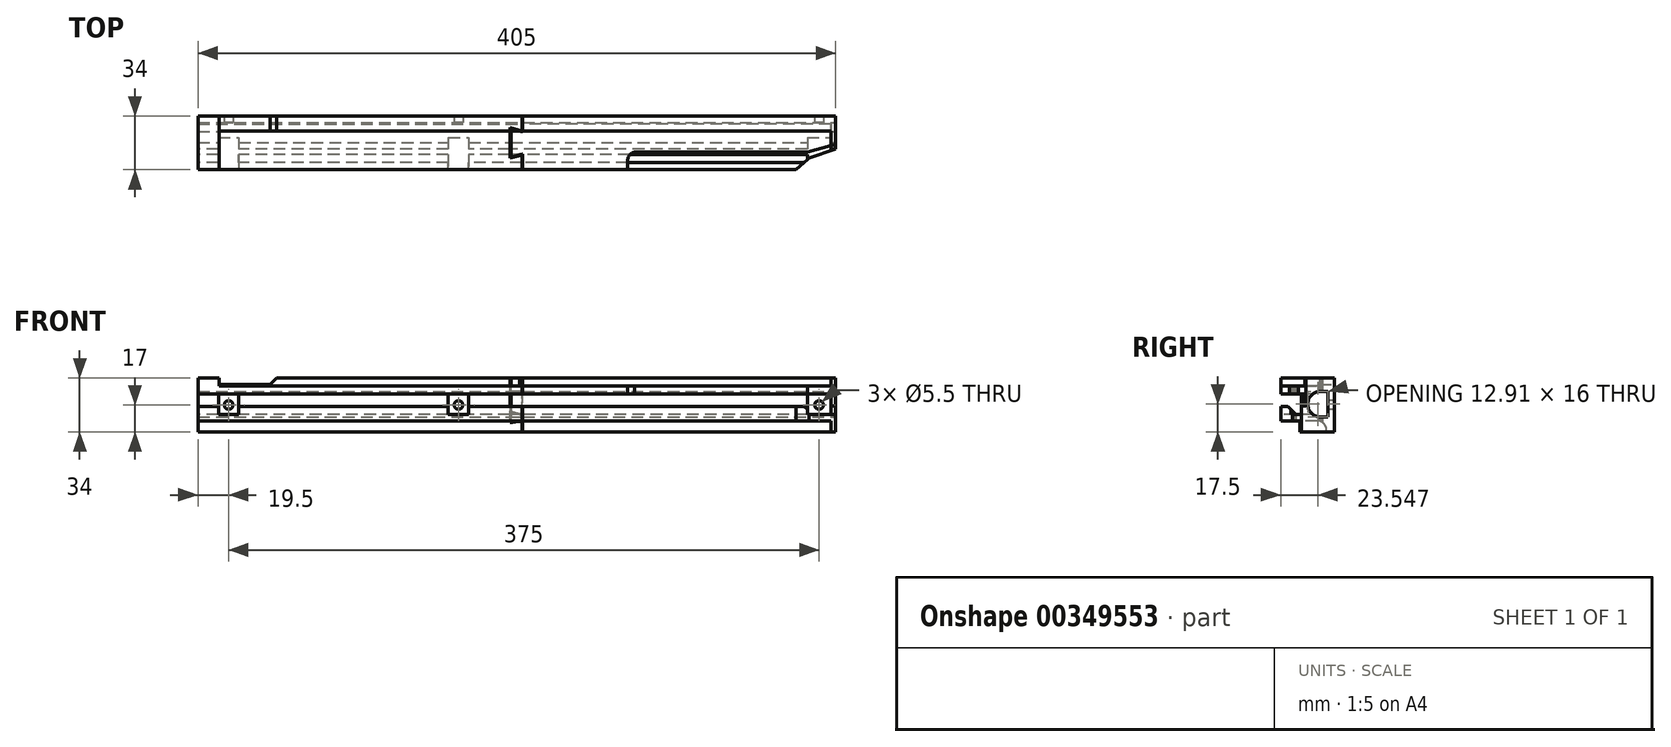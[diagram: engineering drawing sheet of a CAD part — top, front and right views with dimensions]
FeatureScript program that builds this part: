
annotation { "Feature Type Name" : "Feature", "Feature Type Description" : "" }
export const myFeature = defineFeature(function(context is Context, id is Id, definition is map)
    precondition{}
    {
        {
            var Q0;
            Q0=qCreatedBy(makeId("Front.planeOp"),FACE);
            var sketch = newSketch(context, id + "F0", { "sketchPlane" : qUnion([Q0])});
            skLineSegment(sketch, "E0.bottom", {"start": v(202.5, -17) * mm, "end": v(-202.5, -17) * mm});
            skLineSegment(sketch, "E0.top", {"start": v(202.5, 17) * mm, "end": v(-202.5, 17) * mm});
            skLineSegment(sketch, "E0.left", {"start": v(202.5, -17) * mm, "end": v(202.5, 17) * mm});
            skLineSegment(sketch, "E0.right", {"start": v(-202.5, -17) * mm, "end": v(-202.5, 17) * mm});
            skPoint(sketch, "E0.middle", {"position": v(0, 0) * mm});
            skSolve(sketch);
        }
        {
            var Q0;
            Q0 = qSketchRegion(id + "F0", true);
            extrude(context, id + "F1", {"entities" : qUnion([Q0]), "depth" : 34 * mm});
        }
        {
            var Q0;
            Q0=makeQuery(id+"F1.opExtrude","CAP_FACE",FACE,{"disambiguationData":[OSD([sQuery(id+"F0.wireOp",EDGE,"E0.bottom"),sQuery(id+"F0.wireOp",EDGE,"E0.top"),sQuery(id+"F0.wireOp",EDGE,"E0.left"),sQuery(id+"F0.wireOp",EDGE,"E0.right")])],"isStart":false});
            var sketch = newSketch(context, id + "F2", { "sketchPlane" : qUnion([Q0])});
            skLineSegment(sketch, "E1.bottom", {"start": v(-202.5, -17) * mm, "end": v(199.5, -17) * mm});
            skLineSegment(sketch, "E1.top", {"start": v(-202.5, -10) * mm, "end": v(199.5, -10) * mm});
            skLineSegment(sketch, "E1.left", {"start": v(-202.5, -17) * mm, "end": v(-202.5, -10) * mm});
            skLineSegment(sketch, "E2", {"start": v(199.5, -10) * mm, "end": v(199.5, -17) * mm});
            skSolve(sketch);
        }
        {
            var Q0;
            Q0 = qSketchRegion(id + "F2", true);
            extrude(context, id + "F3", {"entities" : qUnion([Q0]), "operationType" : NewBodyOperationType.REMOVE, "oppositeDirection" : true, "depth" : 29 * mm});
        }
        {
            var Q0;
            Q0=makeQuery(id+"F1.opExtrude","CAP_FACE",FACE,{"disambiguationData":[OSD([sQuery(id+"F0.wireOp",EDGE,"E0.bottom"),sQuery(id+"F0.wireOp",EDGE,"E0.top"),sQuery(id+"F0.wireOp",EDGE,"E0.left"),sQuery(id+"F0.wireOp",EDGE,"E0.right")])],"isStart":false});
            var sketch = newSketch(context, id + "F4", { "sketchPlane" : qUnion([Q0])});
            skLineSegment(sketch, "E3.bottom", {"start": v(-189, 17) * mm, "end": v(193, 17) * mm});
            skLineSegment(sketch, "E3.top", {"start": v(-189, 12) * mm, "end": v(193, 12) * mm});
            skLineSegment(sketch, "E3.left", {"start": v(-189, 17) * mm, "end": v(-189, 12) * mm});
            skLineSegment(sketch, "E3.right", {"start": v(193, 17) * mm, "end": v(193, 12) * mm});
            skSolve(sketch);
        }
        {
            var Q0;
            Q0 = qSketchRegion(id + "F4", true);
            extrude(context, id + "F5", {"entities" : qUnion([Q0]), "operationType" : NewBodyOperationType.REMOVE, "oppositeDirection" : true, "depth" : 24.5 * mm});
        }
        {
            var Q0;
            Q0=makeQuery(id+"F3.boolean.opBoolean","COPY",EDGE,{"derivedFrom":makeQuery(id+"F3.opExtrude","CAP_EDGE",EDGE,{"disambiguationData":[OSD([sQuery(id+"F2.wireOp",EDGE,"E1.top")])],"isStart":false})});
            fillet(context, id + "F6", {"entities" : qUnion([Q0]), "radius" : 6 * mm, "tangentPropagation" : true, "allowEdgeOverflow" : false});
        }
        {
            var Q0;
            Q0=makeQuery(id+"F1.opExtrude","SWEPT_FACE",FACE,{"disambiguationData":[OSD([sQuery(id+"F0.wireOp",EDGE,"E0.right")])]});
            var sketch = newSketch(context, id + "F7", { "sketchPlane" : qUnion([Q0])});
            skLineSegment(sketch, "E4", {"start": v(34, 7) * mm, "end": v(21, 7) * mm});
            skLineSegment(sketch, "E5", {"start": v(21, 7) * mm, "end": v(21, -6) * mm});
            skLineSegment(sketch, "E6", {"start": v(21, -6) * mm, "end": v(24.5, -6) * mm});
            skLineSegment(sketch, "E7", {"start": v(24.5, -6) * mm, "end": v(29.5, -1) * mm});
            skLineSegment(sketch, "E8", {"start": v(34, -1) * mm, "end": v(29.5, -1) * mm});
            skLineSegment(sketch, "E9", {"start": v(34, 7) * mm, "end": v(34, -1) * mm});
            skSolve(sketch);
        }
        {
            var Q0;
            Q0 = qSketchRegion(id + "F7", true);
            extrude(context, id + "F8", {"entities" : qUnion([Q0]), "operationType" : NewBodyOperationType.REMOVE, "endBound" : BoundingType.THROUGH_ALL, "oppositeDirection" : true, "depth" : 25 * mm});
        }
        {
            var Q0;
            Q0=makeQuery(id+"F1.opExtrude","CAP_FACE",FACE,{"disambiguationData":[OSD([sQuery(id+"F0.wireOp",EDGE,"E0.bottom"),sQuery(id+"F0.wireOp",EDGE,"E0.top"),sQuery(id+"F0.wireOp",EDGE,"E0.left"),sQuery(id+"F0.wireOp",EDGE,"E0.right")])],"isStart":true});
            var sketch = newSketch(context, id + "F9", { "sketchPlane" : qUnion([Q0])});
            skLineSegment(sketch, "E10.bottom", {"start": v(189, 17) * mm, "end": v(155.21, 17) * mm});
            skLineSegment(sketch, "E10.top", {"start": v(189, 13) * mm, "end": v(156.5, 13) * mm});
            skLineSegment(sketch, "E10.left", {"start": v(189, 17) * mm, "end": v(189, 13) * mm});
            skLineSegment(sketch, "E11", {"start": v(156.5, 13) * mm, "end": v(152.5, 17) * mm});
            skLineSegment(sketch, "E12", {"start": v(155.21, 17) * mm, "end": v(152.5, 17) * mm});
            skSolve(sketch);
        }
        {
            var Q0;
            Q0 = qSketchRegion(id + "F9", true);
            extrude(context, id + "F10", {"entities" : qUnion([Q0]), "operationType" : NewBodyOperationType.REMOVE, "endBound" : BoundingType.THROUGH_ALL, "oppositeDirection" : true, "depth" : 25 * mm});
        }
        {
            var Q0;
            {var subQ0=sQuery(id+"F0.wireOp",EDGE,"E0.left");var subQ1=sQuery(id+"F0.wireOp",EDGE,"E0.right");var subQ2=sQuery(id+"F0.wireOp",EDGE,"E0.bottom");Q0=makeQuery(id+"F8.boolean.opBoolean","SPLIT",FACE,{"disambiguationData":[TD([makeQuery(id+"F1.opExtrude","SWEPT_FACE",FACE,{"disambiguationData":[OSD([subQ2])]})])],"derivedFrom":makeQuery(id+"F1.opExtrude","CAP_FACE",FACE,{"disambiguationData":[OSD([subQ2,sQuery(id+"F0.wireOp",EDGE,"E0.top"),subQ0,subQ1])],"isStart":false})});}
            var sketch = newSketch(context, id + "F11", { "sketchPlane" : qUnion([Q0])});
            skLineSegment(sketch, "E13.bottom", {"start": v(-189.5, 7) * mm, "end": v(-176.5, 7) * mm});
            skLineSegment(sketch, "E13.top", {"start": v(-189.5, -6) * mm, "end": v(-176.5, -6) * mm});
            skLineSegment(sketch, "E13.left", {"start": v(-189.5, 7) * mm, "end": v(-189.5, -6) * mm});
            skLineSegment(sketch, "E13.right", {"start": v(-176.5, 7) * mm, "end": v(-176.5, -6) * mm});
            skSolve(sketch);
        }
        {
            var Q0;
            Q0 = qSketchRegion(id + "F11", true);
            extrude(context, id + "F12", {"entities" : qUnion([Q0]), "operationType" : NewBodyOperationType.REMOVE, "oppositeDirection" : true, "depth" : 30 * mm});
        }
        {
            var Q0;
            Q0=makeQuery(id+"F12.boolean.opBoolean","COPY",FACE,{"derivedFrom":makeQuery(id+"F12.opExtrude","CAP_FACE",FACE,{"disambiguationData":[OSD([sQuery(id+"F11.wireOp",EDGE,"E13.bottom"),sQuery(id+"F11.wireOp",EDGE,"E13.top"),sQuery(id+"F11.wireOp",EDGE,"E13.left"),sQuery(id+"F11.wireOp",EDGE,"E13.right")])],"isStart":false})});
            var sketch = newSketch(context, id + "F13", { "sketchPlane" : qUnion([Q0])});
            skLineSegment(sketch, "E14", {"start": v(-176.5, -6) * mm, "end": v(-176.5, 7) * mm, "construction": true});
            skLineSegment(sketch, "E15", {"start": v(-176.5, 0) * mm, "end": v(-185.96, 0) * mm, "construction": true});
            skPoint(sketch, "E16.trimOffspring.end.orphan", {"position": v(-189.5, -6) * mm});
            skPoint(sketch, "E17.orphan", {"position": v(-172.63, 0) * mm});
            skLineSegment(sketch, "E18", {"start": v(-185.96, 0) * mm, "end": v(-189.5, 0) * mm, "construction": true});
            skPoint(sketch, "E19.start.orphan", {"position": v(-183, 0.5) * mm});
            skCircle(sketch, "E20", {"center": v(-183, 0) * mm, "radius": 2.75 * mm});
            skSolve(sketch);
        }
        {
            var Q0;
            Q0 = qSketchRegion(id + "F13", true);
            extrude(context, id + "F14", {"entities" : qUnion([Q0]), "operationType" : NewBodyOperationType.REMOVE, "endBound" : BoundingType.THROUGH_ALL, "oppositeDirection" : true, "depth" : 25 * mm});
        }
        {
            var Q0;
            {var subQ0=sQuery(id+"F0.wireOp",EDGE,"E0.left");var subQ1=sQuery(id+"F0.wireOp",EDGE,"E0.right");var subQ2=sQuery(id+"F0.wireOp",EDGE,"E0.bottom");Q0=makeQuery(id+"F8.boolean.opBoolean","SPLIT",FACE,{"disambiguationData":[TD([makeQuery(id+"F1.opExtrude","SWEPT_FACE",FACE,{"disambiguationData":[OSD([subQ2])]})])],"derivedFrom":makeQuery(id+"F1.opExtrude","CAP_FACE",FACE,{"disambiguationData":[OSD([subQ2,sQuery(id+"F0.wireOp",EDGE,"E0.top"),subQ0,subQ1])],"isStart":false})});}
            var sketch = newSketch(context, id + "F15", { "sketchPlane" : qUnion([Q0])});
            skLineSegment(sketch, "E21.bottom", {"start": v(-43.5, -6) * mm, "end": v(-30.5, -6) * mm});
            skLineSegment(sketch, "E21.top", {"start": v(-43.5, 7) * mm, "end": v(-30.5, 7) * mm});
            skLineSegment(sketch, "E21.left", {"start": v(-43.5, -6) * mm, "end": v(-43.5, 7) * mm});
            skLineSegment(sketch, "E21.right", {"start": v(-30.5, -6) * mm, "end": v(-30.5, 7) * mm});
            skSolve(sketch);
        }
        {
            var Q0;
            Q0 = qSketchRegion(id + "F15", true);
            extrude(context, id + "F16", {"entities" : qUnion([Q0]), "operationType" : NewBodyOperationType.REMOVE, "oppositeDirection" : true, "depth" : 29 * mm});
        }
        {
            var Q0;
            Q0=makeQuery(id+"F16.boolean.opBoolean","COPY",FACE,{"derivedFrom":makeQuery(id+"F16.opExtrude","CAP_FACE",FACE,{"disambiguationData":[OSD([sQuery(id+"F15.wireOp",EDGE,"E21.bottom"),sQuery(id+"F15.wireOp",EDGE,"E21.top"),sQuery(id+"F15.wireOp",EDGE,"E21.left"),sQuery(id+"F15.wireOp",EDGE,"E21.right")])],"isStart":false})});
            var sketch = newSketch(context, id + "F17", { "sketchPlane" : qUnion([Q0])});
            skLineSegment(sketch, "E22", {"start": v(-30.5, -6) * mm, "end": v(-30.5, 7) * mm, "construction": true});
            skLineSegment(sketch, "E23", {"start": v(-30.5, 0) * mm, "end": v(-43.5, 0) * mm, "construction": true});
            skPoint(sketch, "E24.start.orphan", {"position": v(-43.5, 7) * mm});
            skPoint(sketch, "E25.center.orphan", {"position": v(-37, 0.5) * mm});
            skCircle(sketch, "E26", {"center": v(-37, 0) * mm, "radius": 2.75 * mm});
            skSolve(sketch);
        }
        {
            var Q0;
            Q0 = qSketchRegion(id + "F17", true);
            extrude(context, id + "F18", {"entities" : qUnion([Q0]), "operationType" : NewBodyOperationType.REMOVE, "endBound" : BoundingType.THROUGH_ALL, "oppositeDirection" : true, "depth" : 25 * mm});
        }
        {
            var Q0;
            {var subQ0=sQuery(id+"F0.wireOp",EDGE,"E0.left");var subQ1=sQuery(id+"F0.wireOp",EDGE,"E0.right");var subQ2=sQuery(id+"F0.wireOp",EDGE,"E0.bottom");Q0=makeQuery(id+"F8.boolean.opBoolean","SPLIT",FACE,{"disambiguationData":[TD([makeQuery(id+"F1.opExtrude","SWEPT_FACE",FACE,{"disambiguationData":[OSD([subQ2])]})])],"derivedFrom":makeQuery(id+"F1.opExtrude","CAP_FACE",FACE,{"disambiguationData":[OSD([subQ2,sQuery(id+"F0.wireOp",EDGE,"E0.top"),subQ0,subQ1])],"isStart":false})});}
            var sketch = newSketch(context, id + "F19", { "sketchPlane" : qUnion([Q0])});
            skLineSegment(sketch, "E27.bottom", {"start": v(199.5, 7) * mm, "end": v(184.5, 7) * mm});
            skLineSegment(sketch, "E27.top", {"start": v(199.5, -6) * mm, "end": v(184.5, -6) * mm});
            skLineSegment(sketch, "E27.left", {"start": v(199.5, 7) * mm, "end": v(199.5, -6) * mm});
            skLineSegment(sketch, "E27.right", {"start": v(184.5, 7) * mm, "end": v(184.5, -6) * mm});
            skSolve(sketch);
        }
        {
            var Q0;
            Q0 = qSketchRegion(id + "F19", true);
            extrude(context, id + "F20", {"entities" : qUnion([Q0]), "operationType" : NewBodyOperationType.REMOVE, "oppositeDirection" : true, "depth" : 29 * mm});
        }
        {
            var Q0;
            Q0=makeQuery(id+"F20.boolean.opBoolean","COPY",FACE,{"derivedFrom":makeQuery(id+"F20.opExtrude","CAP_FACE",FACE,{"disambiguationData":[OSD([sQuery(id+"F19.wireOp",EDGE,"E27.bottom"),sQuery(id+"F19.wireOp",EDGE,"E27.top"),sQuery(id+"F19.wireOp",EDGE,"E27.left"),sQuery(id+"F19.wireOp",EDGE,"E27.right")])],"isStart":false})});
            var sketch = newSketch(context, id + "F21", { "sketchPlane" : qUnion([Q0])});
            skLineSegment(sketch, "E28", {"start": v(199.5, -6) * mm, "end": v(199.5, 7) * mm, "construction": true});
            skLineSegment(sketch, "E29", {"start": v(184.5, 0) * mm, "end": v(199.5, 0) * mm, "construction": true});
            skPoint(sketch, "E30.orphan", {"position": v(184.5, -6) * mm});
            skPoint(sketch, "E31.trimOffspring.start.orphan", {"position": v(192, 0.5) * mm});
            skCircle(sketch, "E32", {"center": v(192, 0) * mm, "radius": 2.75 * mm});
            skSolve(sketch);
        }
        {
            var Q0;
            Q0 = qSketchRegion(id + "F21", true);
            extrude(context, id + "F22", {"entities" : qUnion([Q0]), "operationType" : NewBodyOperationType.REMOVE, "endBound" : BoundingType.THROUGH_ALL, "oppositeDirection" : true, "depth" : 25 * mm});
        }
        {
            var Q0;
            Q0=makeQuery(id+"F5.boolean.opBoolean","COPY",FACE,{"derivedFrom":makeQuery(id+"F5.opExtrude","SWEPT_FACE",FACE,{"disambiguationData":[OSD([sQuery(id+"F4.wireOp",EDGE,"E3.top")])]})});
            var sketch = newSketch(context, id + "F23", { "sketchPlane" : qUnion([Q0])});
            skLineSegment(sketch, "E33", {"start": v(70.5, -34) * mm, "end": v(70.5, -27.4) * mm});
            skLineSegment(sketch, "E34", {"start": v(74.78, -23) * mm, "end": v(184.5, -23) * mm});
            skLineSegment(sketch, "E35", {"start": v(184.5, -23) * mm, "end": v(202.5, -18) * mm});
            skLineSegment(sketch, "E36", {"start": v(202.5, -18) * mm, "end": v(202.5, -34) * mm});
            skLineSegment(sketch, "E37", {"start": v(202.5, -34) * mm, "end": v(70.5, -34) * mm});
            skArc(sketch, "E38", {"start": v(74.78, -23) * mm, "mid": v(71.52, -24.88) * mm, "end": v(70.5, -28.5) * mm});
            skPoint(sketch, "E39.orphan", {"position": v(70.5, -23) * mm});
            skSolve(sketch);
        }
        {
            var Q0;
            Q0 = qSketchRegion(id + "F23", true);
            extrude(context, id + "F24", {"entities" : qUnion([Q0]), "operationType" : NewBodyOperationType.REMOVE, "endBound" : BoundingType.SYMMETRIC, "depth" : 25 * mm});
        }
        {
            var Q0;
            {var subQ0=sQuery(id+"F0.wireOp",EDGE,"E0.left");var subQ3=makeQuery(id+"F8.boolean.opBoolean","COPY",FACE,{"derivedFrom":makeQuery(id+"F8.opExtrude","SWEPT_FACE",FACE,{"disambiguationData":[OSD([sQuery(id+"F7.wireOp",EDGE,"E8")])]})});var subQ5=makeQuery(id+"F1.opExtrude","SWEPT_FACE",FACE,{"disambiguationData":[OSD([subQ0])]});Q0=makeQuery(id+"F20.boolean.opBoolean","SPLIT",FACE,{"disambiguationData":[TD([makeQuery(id+"F20.opExtrude","SWEPT_FACE",FACE,{"disambiguationData":[OSD([sQuery(id+"F19.wireOp",EDGE,"E27.right")])]})])],"derivedFrom":makeQuery(id+"F16.boolean.opBoolean","SPLIT",FACE,{"disambiguationData":[TD([subQ5])],"derivedFrom":makeQuery(id+"F12.boolean.opBoolean","SPLIT",FACE,{"disambiguationData":[TD([subQ5])],"derivedFrom":subQ3})})});}
            var sketch = newSketch(context, id + "F25", { "sketchPlane" : qUnion([Q0])});
            skLineSegment(sketch, "E40", {"start": v(177.5, -34) * mm, "end": v(185.5, -26.62) * mm});
            skLineSegment(sketch, "E41", {"start": v(185.5, -26.62) * mm, "end": v(202.5, -21) * mm});
            skLineSegment(sketch, "E42", {"start": v(202.5, -21) * mm, "end": v(202.5, -34) * mm});
            skLineSegment(sketch, "E43", {"start": v(202.5, -34) * mm, "end": v(177.5, -34) * mm});
            skSolve(sketch);
        }
        {
            var Q0;
            Q0 = qSketchRegion(id + "F25", true);
            extrude(context, id + "F26", {"entities" : qUnion([Q0]), "operationType" : NewBodyOperationType.REMOVE, "oppositeDirection" : true, "depth" : 25 * mm});
        }
        {
            var Q0;
            Q0=makeQuery(id+"F5.boolean.opBoolean","COPY",FACE,{"derivedFrom":makeQuery(id+"F5.opExtrude","CAP_FACE",FACE,{"disambiguationData":[OSD([sQuery(id+"F4.wireOp",EDGE,"E3.bottom"),sQuery(id+"F4.wireOp",EDGE,"E3.top"),sQuery(id+"F4.wireOp",EDGE,"E3.left"),sQuery(id+"F4.wireOp",EDGE,"E3.right")])],"isStart":false})});
            var sketch = newSketch(context, id + "F27", { "sketchPlane" : qUnion([Q0])});
            skLineSegment(sketch, "E44.bottom", {"start": v(193, 17) * mm, "end": v(199.5, 17) * mm});
            skLineSegment(sketch, "E44.top", {"start": v(193, 12) * mm, "end": v(199.5, 12) * mm});
            skLineSegment(sketch, "E44.left", {"start": v(193, 17) * mm, "end": v(193, 12) * mm});
            skLineSegment(sketch, "E44.right", {"start": v(199.5, 17) * mm, "end": v(199.5, 12) * mm});
            skSolve(sketch);
        }
        {
            var Q0;
            Q0 = qSketchRegion(id + "F27", true);
            extrude(context, id + "F28", {"entities" : qUnion([Q0]), "operationType" : NewBodyOperationType.REMOVE, "depth" : 25 * mm});
        }
        {
            var Q0;
            Q0=makeQuery(id+"F28.boolean.opBoolean","MERGE",EDGE,{"derivedFrom":[makeQuery(id+"F5.boolean.opBoolean","COPY",EDGE,{"derivedFrom":makeQuery(id+"F5.opExtrude","CAP_EDGE",EDGE,{"disambiguationData":[OSD([sQuery(id+"F4.wireOp",EDGE,"E3.top")])],"isStart":false})}),makeQuery(id+"F28.opExtrude","CAP_EDGE",EDGE,{"disambiguationData":[OSD([sQuery(id+"F27.wireOp",EDGE,"E44.top")])],"isStart":true})]});
            fillet(context, id + "F29", {"entities" : qUnion([Q0]), "radius" : 1 * mm, "tangentPropagation" : true, "allowEdgeOverflow" : false});
        }
        {
            var Q0;
            Q0=makeQuery(id+"F1.opExtrude","SWEPT_FACE",FACE,{"disambiguationData":[OSD([sQuery(id+"F0.wireOp",EDGE,"E0.left")])]});
            var sketch = newSketch(context, id + "F30", { "sketchPlane" : qUnion([Q0])});
            skLineSegment(sketch, "E45.0", {"start": v(-4, -6) * mm, "end": v(-4, 7) * mm});
            skLineSegment(sketch, "E46.0", {"start": v(-11.33, 7) * mm, "end": v(-11.33, 7) * mm});
            skPoint(sketch, "E47.orphan", {"position": v(-21, 7) * mm});
            skPoint(sketch, "E48.orphan", {"position": v(-21, -6) * mm});
            skPoint(sketch, "E49.orphan", {"position": v(-4, 7) * mm});
            skPoint(sketch, "E50.orphan", {"position": v(-4, -6) * mm});
            skLineSegment(sketch, "E51", {"start": v(-4, 7) * mm, "end": v(-4, 8.5) * mm});
            skLineSegment(sketch, "E52", {"start": v(-4, -6) * mm, "end": v(-4, -7.5) * mm});
            skLineSegment(sketch, "E53", {"start": v(-4, 8.5) * mm, "end": v(-9.85, 8.5) * mm});
            skLineSegment(sketch, "E54", {"start": v(-9.85, -7.5) * mm, "end": v(-4, -7.5) * mm});
            skArc(sketch, "E55", {"start": v(-9.85, 8.5) * mm, "mid": v(-16.9, 0.5) * mm, "end": v(-9.85, -7.5) * mm});
            skSolve(sketch);
        }
        {
            var Q0;
            Q0 = qSketchRegion(id + "F30", true);
            extrude(context, id + "F31", {"entities" : qUnion([Q0]), "operationType" : NewBodyOperationType.REMOVE, "endBound" : BoundingType.THROUGH_ALL, "oppositeDirection" : true, "depth" : 25 * mm});
        }
        {
            var Q0;
            Q0=qCreatedBy(makeId("Top.planeOp"),FACE);
            var sketch = newSketch(context, id + "F32", { "sketchPlane" : qUnion([Q0])});
            skLineSegment(sketch, "E56.left", {"start": v(-3.74, -26) * mm, "end": v(-3.75, -8) * mm});
            skLineSegment(sketch, "E56.right", {"start": v(3.76, -34) * mm, "end": v(3.75, -24) * mm});
            skPoint(sketch, "E56.middle", {"position": v(0, 0) * mm});
            skPoint(sketch, "E56.top.end.orphan", {"position": v(3.74, 34) * mm});
            skPoint(sketch, "E56.top.start.orphan", {"position": v(-3.76, 34) * mm});
            skLineSegment(sketch, "E57", {"start": v(3.75, -24) * mm, "end": v(-3.74, -26) * mm});
            skLineSegment(sketch, "E58", {"start": v(3.75, -10) * mm, "end": v(-3.75, -8) * mm});
            skLineSegment(sketch, "E59.trimOffspring", {"start": v(3.75, -10) * mm, "end": v(3.75, 0) * mm});
            skPoint(sketch, "E56.bottom.start.orphan", {"position": v(-3.74, -34) * mm});
            skPoint(sketch, "E60.end.orphan", {"position": v(-3.75, 0) * mm});
            skLineSegment(sketch, "E61.0", {"start": v(3.25, -9.35) * mm, "end": v(3.25, 0) * mm});
            skLineSegment(sketch, "E61.1", {"start": v(3.26, -34) * mm, "end": v(3.25, -24.65) * mm});
            skLineSegment(sketch, "E61.2", {"start": v(3.25, -24.65) * mm, "end": v(-4.24, -26.65) * mm});
            skLineSegment(sketch, "E61.3", {"start": v(-4.24, -26.65) * mm, "end": v(-4.25, -7.35) * mm});
            skLineSegment(sketch, "E61.4", {"start": v(3.25, -9.35) * mm, "end": v(-4.25, -7.35) * mm});
            skLineSegment(sketch, "E62.1", {"start": v(62.8, -28.99) * mm, "end": v(62.8, -28.72) * mm});
            skLineSegment(sketch, "E62.3", {"start": v(3.26, -29) * mm, "end": v(3.76, -29) * mm});
            skLineSegment(sketch, "E62.8", {"start": v(-3.75, -14.5) * mm, "end": v(-4.25, -14.5) * mm});
            skLineSegment(sketch, "E63", {"start": v(3.75, 0) * mm, "end": v(3.25, 0) * mm});
            skLineSegment(sketch, "E64", {"start": v(3.76, -34) * mm, "end": v(3.26, -34) * mm});
            skSolve(sketch);
        }
        {
            var Q0;
            Q0 = qSketchRegion(id + "F32", true);
            extrude(context, id + "F33", {"entities" : qUnion([Q0]), "operationType" : NewBodyOperationType.REMOVE, "endBound" : BoundingType.SYMMETRIC, "oppositeDirection" : true, "depth" : 35 * mm});
        }
    });
